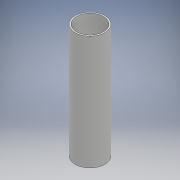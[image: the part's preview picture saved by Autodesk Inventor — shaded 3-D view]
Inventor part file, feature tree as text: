
AUTODESK INVENTOR PART (.ipt)
format: ipt  version: 2017 (Build 210142000, 142)  size: 94,208 bytes
history: native  units: mm
features: extrude x1, sketch x1
ambient origin geometry x8: Origin, YZ Plane, XZ Plane, XY Plane, X Axis, Y Axis, Z Axis, Center Point
bodies: Body1 (feature_tree)
feature tree (2):
  extrude  "Extrusion2"  Depth=84.915mm
  sketch  "Sketch2"  dims[d5=22.0mm d7=1.0mm d8=84.915mm d9=0.0mm]
